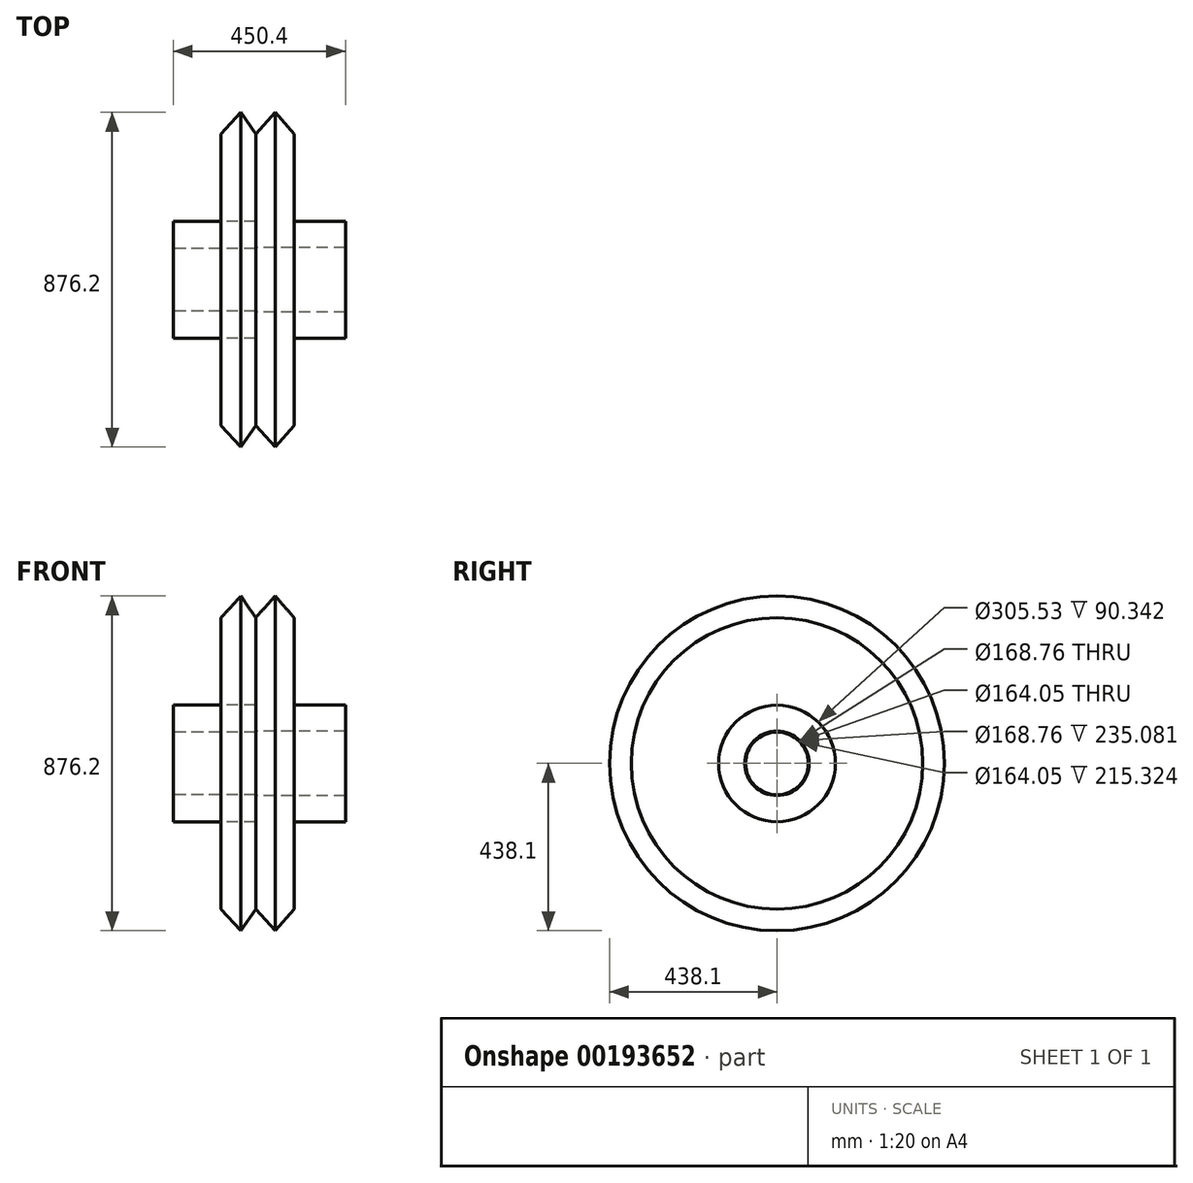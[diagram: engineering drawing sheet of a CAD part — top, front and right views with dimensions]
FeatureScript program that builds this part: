
annotation { "Feature Type Name" : "Feature", "Feature Type Description" : "" }
export const myFeature = defineFeature(function(context is Context, id is Id, definition is map)
    precondition{}
    {
        {
            var Q0;
            Q0=qCreatedBy(makeId("Top.planeOp"),FACE);
            var sketch = newSketch(context, id + "F0", { "sketchPlane" : qUnion([Q0])});
            skLineSegment(sketch, "E0", {"start": v(0, 0) * mm, "end": v(232.72, 0) * mm});
            skLineSegment(sketch, "E1.bottom", {"start": v(0, 84.38) * mm, "end": v(235.08, 84.38) * mm});
            skLineSegment(sketch, "E1.top", {"start": v(0, 152.77) * mm, "end": v(235.08, 152.77) * mm});
            skLineSegment(sketch, "E1.left", {"start": v(0, 84.38) * mm, "end": v(0, 152.77) * mm});
            skLineSegment(sketch, "E1.right", {"start": v(235.08, 84.38) * mm, "end": v(235.08, 152.77) * mm});
            skLineSegment(sketch, "E2.bottom", {"start": v(0, 84.38) * mm, "end": v(100.67, 84.38) * mm});
            skLineSegment(sketch, "E2.top", {"start": v(0, 381.5) * mm, "end": v(100.67, 381.5) * mm});
            skLineSegment(sketch, "E2.left", {"start": v(0, 84.38) * mm, "end": v(0, 381.5) * mm});
            skLineSegment(sketch, "E2.right", {"start": v(100.67, 84.38) * mm, "end": v(100.67, 381.5) * mm});
            skLineSegment(sketch, "E3", {"start": v(0, 0) * mm, "end": v(-212.97, 0) * mm});
            skLineSegment(sketch, "E4.bottom", {"start": v(0, 152.77) * mm, "end": v(-215.32, 152.77) * mm});
            skLineSegment(sketch, "E4.top", {"start": v(0, 82.02) * mm, "end": v(-215.32, 82.02) * mm});
            skLineSegment(sketch, "E4.left", {"start": v(0, 152.77) * mm, "end": v(0, 82.02) * mm});
            skLineSegment(sketch, "E4.right", {"start": v(-215.32, 152.77) * mm, "end": v(-215.32, 82.02) * mm});
            skLineSegment(sketch, "E5.bottom", {"start": v(0, 381.5) * mm, "end": v(-90.34, 381.5) * mm});
            skLineSegment(sketch, "E5.top", {"start": v(0, 82.02) * mm, "end": v(-90.34, 82.02) * mm});
            skLineSegment(sketch, "E5.left", {"start": v(0, 381.5) * mm, "end": v(0, 82.02) * mm});
            skLineSegment(sketch, "E5.right", {"start": v(-90.34, 381.5) * mm, "end": v(-90.34, 82.02) * mm});
            skLineSegment(sketch, "E6", {"start": v(-90.34, 381.5) * mm, "end": v(-38.46, 438.1) * mm});
            skLineSegment(sketch, "E7", {"start": v(-38.46, 438.1) * mm, "end": v(0, 381.5) * mm});
            skLineSegment(sketch, "E8", {"start": v(51.15, 438.1) * mm, "end": v(100.67, 381.5) * mm});
            skLineSegment(sketch, "E9", {"start": v(51.15, 438.1) * mm, "end": v(0, 381.5) * mm});
            skLineSegment(sketch, "E10.MirrorCS", {"start": v(-90.34, -381.5) * mm, "end": v(-38.46, -438.1) * mm});
            skLineSegment(sketch, "E11.MirrorCS", {"start": v(51.15, -438.1) * mm, "end": v(100.67, -381.5) * mm});
            skLineSegment(sketch, "E12.MirrorCS", {"start": v(0, -381.5) * mm, "end": v(-90.34, -381.5) * mm});
            skLineSegment(sketch, "E13.MirrorCS", {"start": v(0, -84.38) * mm, "end": v(235.08, -84.38) * mm});
            skLineSegment(sketch, "E14.MirrorCS", {"start": v(0, -152.77) * mm, "end": v(235.08, -152.77) * mm});
            skLineSegment(sketch, "E15.MirrorCS", {"start": v(235.08, -84.38) * mm, "end": v(235.08, -152.77) * mm});
            skLineSegment(sketch, "E16.MirrorCS", {"start": v(100.67, -84.38) * mm, "end": v(100.67, -381.5) * mm});
            skLineSegment(sketch, "E17.MirrorCS", {"start": v(0, -84.38) * mm, "end": v(100.67, -84.38) * mm});
            skLineSegment(sketch, "E18.MirrorCS", {"start": v(0, -381.5) * mm, "end": v(0, -82.02) * mm});
            skLineSegment(sketch, "E19.MirrorCS", {"start": v(0, -381.5) * mm, "end": v(100.67, -381.5) * mm});
            skLineSegment(sketch, "E20.MirrorCS", {"start": v(51.15, -438.1) * mm, "end": v(0, -381.5) * mm});
            skLineSegment(sketch, "E21.MirrorCS", {"start": v(-90.34, -381.5) * mm, "end": v(-90.34, -82.02) * mm});
            skLineSegment(sketch, "E22.MirrorCS", {"start": v(-38.46, -438.1) * mm, "end": v(0, -381.5) * mm});
            skLineSegment(sketch, "E23.MirrorCS", {"start": v(0, -152.77) * mm, "end": v(-215.32, -152.77) * mm});
            skLineSegment(sketch, "E24.MirrorCS", {"start": v(0, -82.02) * mm, "end": v(-215.32, -82.02) * mm});
            skLineSegment(sketch, "E25.MirrorCS", {"start": v(-215.32, -152.77) * mm, "end": v(-215.32, -82.02) * mm});
            skSolve(sketch);
        }
        {
            var Q0;
            {var subQ0=sQuery(id+"F0.wireOp",EDGE,"E12.MirrorCS");Q0=makeQuery(id+"F0.imprint","IMPRINT",FACE,{"disambiguationData":[TD([[makeQuery(id+"F0.imprint","IMPRINT",EDGE,{"derivedFrom":subQ0}),-1.0]])]});}
            var Q1;
            {var subQ5=sQuery(id+"F0.wireOp",EDGE,"E19.MirrorCS");Q1=makeQuery(id+"F0.imprint","IMPRINT",FACE,{"disambiguationData":[TD([[makeQuery(id+"F0.imprint","IMPRINT",EDGE,{"derivedFrom":subQ5}),1.0]])]});}
            var Q2;
            Q2=makeQuery(id+"F0.imprint","IMPRINT",FACE,{"disambiguationData":[TD([[makeQuery(id+"F0.imprint","IMPRINT",EDGE,{"derivedFrom":sQuery(id+"F0.wireOp",EDGE,"E10.MirrorCS")}),1.0]])]});
            var Q3;
            Q3=makeQuery(id+"F0.imprint","IMPRINT",FACE,{"disambiguationData":[TD([[makeQuery(id+"F0.imprint","IMPRINT",EDGE,{"derivedFrom":sQuery(id+"F0.wireOp",EDGE,"E19.MirrorCS")}),-1.0]])]});
            var Q4;
            {var subQ5=sQuery(id+"F0.wireOp",EDGE,"E25.MirrorCS");Q4=makeQuery(id+"F0.imprint","IMPRINT",FACE,{"disambiguationData":[TD([[makeQuery(id+"F0.imprint","IMPRINT",EDGE,{"derivedFrom":subQ5}),-1.0]])]});}
            var Q5;
            {var subQ1=sQuery(id+"F0.wireOp",EDGE,"E18.MirrorCS");var subQ5=makeQuery(id+"F0.imprint","INTERSECT",VERTEX,{"derivedFrom":[sQuery(id+"F0.wireOp",EDGE,"E17.MirrorCS"),subQ1]});Q5=makeQuery(id+"F0.imprint","IMPRINT",FACE,{"disambiguationData":[TD([[makeQuery(id+"F0.imprint","IMPRINT",EDGE,{"disambiguationData":[TD([[subQ5,-1.0]])],"derivedFrom":subQ1}),1.0]])]});}
            var Q6;
            {var subQ5=sQuery(id+"F0.wireOp",EDGE,"E17.MirrorCS");Q6=makeQuery(id+"F0.imprint","IMPRINT",FACE,{"disambiguationData":[TD([[makeQuery(id+"F0.imprint","IMPRINT",EDGE,{"derivedFrom":subQ5}),-1.0]])]});}
            var Q7;
            {var subQ0=sQuery(id+"F0.wireOp",EDGE,"E13.MirrorCS");Q7=makeQuery(id+"F0.imprint","IMPRINT",FACE,{"disambiguationData":[TD([[makeQuery(id+"F0.imprint","IMPRINT",EDGE,{"derivedFrom":subQ0}),-1.0]])]});}
            var Q8;
            {var subQ4=sQuery(id+"F0.wireOp",EDGE,"E4.top");Q8=makeQuery(id+"F0.imprint","IMPRINT",FACE,{"disambiguationData":[TD([[makeQuery(id+"F0.imprint","IMPRINT",EDGE,{"derivedFrom":subQ4}),-1.0]])]});}
            var Q9;
            {var subQ2=sQuery(id+"F0.wireOp",EDGE,"E5.top");Q9=makeQuery(id+"F0.imprint","IMPRINT",FACE,{"disambiguationData":[TD([[makeQuery(id+"F0.imprint","IMPRINT",EDGE,{"derivedFrom":subQ2}),-1.0]])]});}
            var Q10;
            {var subQ5=sQuery(id+"F0.wireOp",EDGE,"E2.bottom");Q10=makeQuery(id+"F0.imprint","IMPRINT",FACE,{"disambiguationData":[TD([[makeQuery(id+"F0.imprint","IMPRINT",EDGE,{"derivedFrom":subQ5}),1.0]])]});}
            var Q11;
            {var subQ0=sQuery(id+"F0.wireOp",EDGE,"E1.bottom");Q11=makeQuery(id+"F0.imprint","IMPRINT",FACE,{"disambiguationData":[TD([[makeQuery(id+"F0.imprint","IMPRINT",EDGE,{"derivedFrom":subQ0}),1.0]])]});}
            var Q12;
            {var subQ5=sQuery(id+"F0.wireOp",EDGE,"E2.top");Q12=makeQuery(id+"F0.imprint","IMPRINT",FACE,{"disambiguationData":[TD([[makeQuery(id+"F0.imprint","IMPRINT",EDGE,{"derivedFrom":subQ5}),-1.0]])]});}
            var Q13;
            Q13=makeQuery(id+"F0.imprint","IMPRINT",FACE,{"disambiguationData":[TD([[makeQuery(id+"F0.imprint","IMPRINT",EDGE,{"derivedFrom":sQuery(id+"F0.wireOp",EDGE,"E5.bottom")}),-1.0]])]});
            var Q14;
            Q14=makeQuery(id+"F0.imprint","IMPRINT",FACE,{"disambiguationData":[TD([[makeQuery(id+"F0.imprint","IMPRINT",EDGE,{"derivedFrom":sQuery(id+"F0.wireOp",EDGE,"E2.top")}),1.0]])]});
            var Q15;
            {var subQ5=sQuery(id+"F0.wireOp",EDGE,"E5.bottom");Q15=makeQuery(id+"F0.imprint","IMPRINT",FACE,{"disambiguationData":[TD([[makeQuery(id+"F0.imprint","IMPRINT",EDGE,{"derivedFrom":subQ5}),1.0]])]});}
            var Q16;
            Q16=sQuery(id+"F0.wireOp",EDGE,"E0");
            revolve(context, id + "F1", {"entities" : qUnion([Q0, Q1, Q2, Q3, Q4, Q5, Q6, Q7, Q8, Q9, Q10, Q11, Q12, Q13, Q14, Q15]), "axis" : qUnion([Q16]), "revolveType" : RevolveType.FULL});
        }
    });
